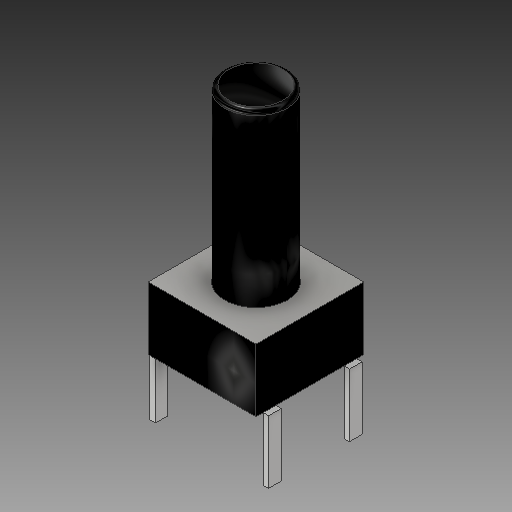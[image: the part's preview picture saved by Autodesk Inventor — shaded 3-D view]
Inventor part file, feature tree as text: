
AUTODESK INVENTOR PART (.ipt)
format: ipt  version: 2019 (Build 230136000, 136)  size: 154,112 bytes
history: native  units: mm
features: extrude x3, sketch x3, other x1, fillet x1
ambient origin geometry x8: Origin, YZ Plane, XZ Plane, XY Plane, X Axis, Y Axis, Z Axis, Center Point
bodies: Solide1 (feature_tree)
feature tree (8):
  other  "Touch Button High"
  extrude  "Extrusion1"  Depth=6.0mm
  extrude  "Extrusion2"  Depth=6.0mm
  fillet  "Congé1"  Radius=3.0mm
  extrude  "Extrusion3"  Depth=3.0mm
  sketch  "Esquisse1"
  sketch  "Esquisse2"
  sketch  "Esquisse3"
